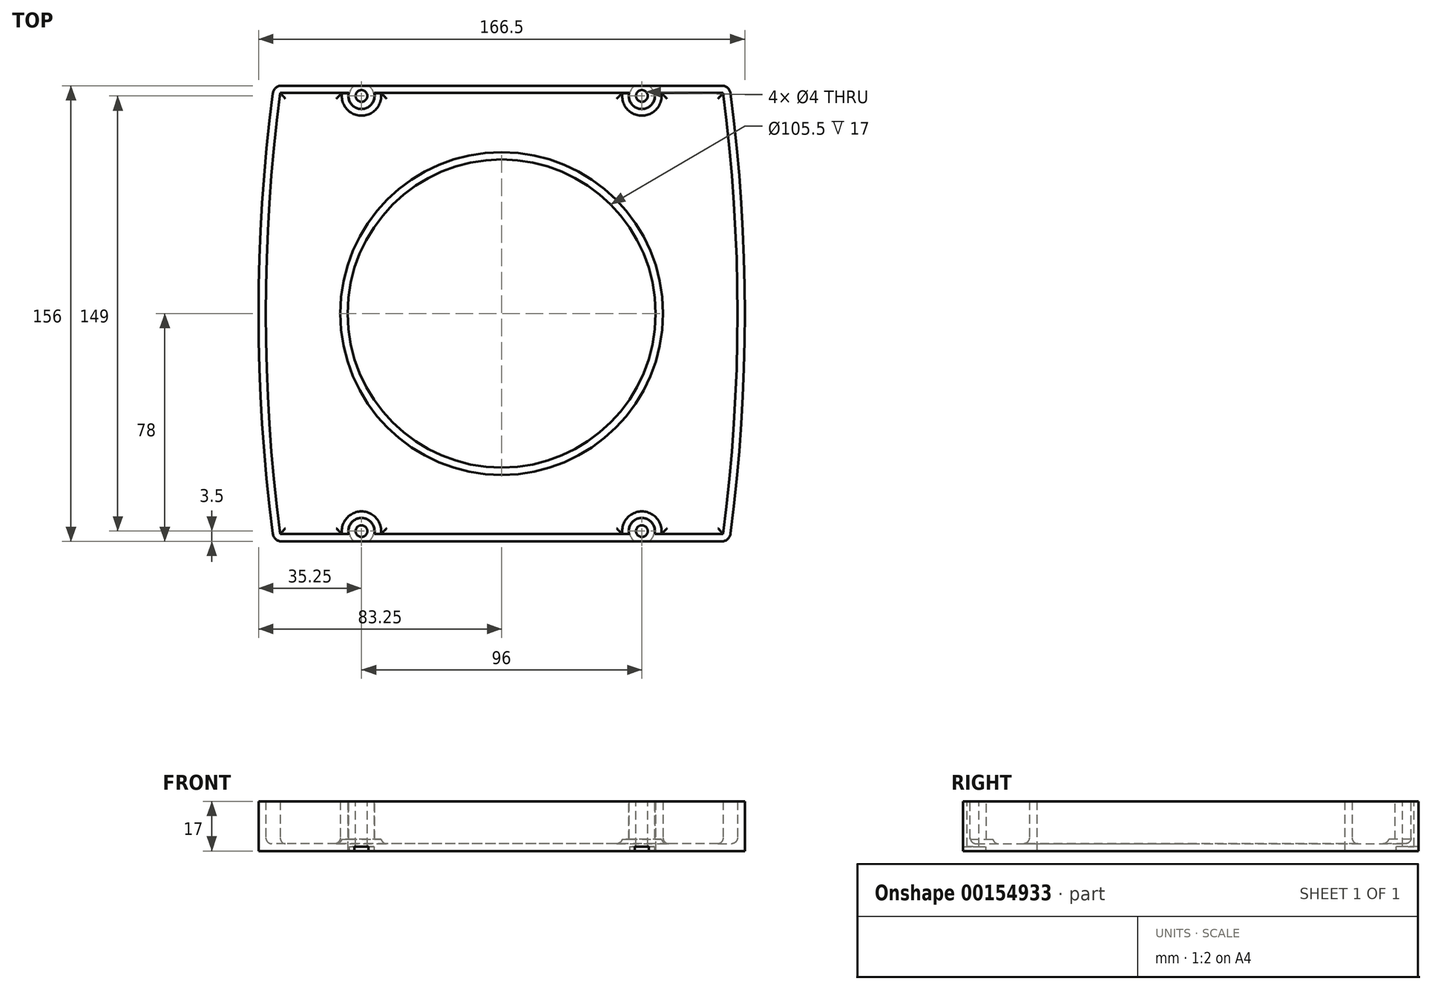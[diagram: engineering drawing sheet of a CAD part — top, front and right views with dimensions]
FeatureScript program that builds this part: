
annotation { "Feature Type Name" : "Feature", "Feature Type Description" : "" }
export const myFeature = defineFeature(function(context is Context, id is Id, definition is map)
    precondition{}
    {
        {
            var Q0;
            Q0=qCreatedBy(makeId("Top.planeOp"),FACE);
            var sketch = newSketch(context, id + "F0", { "sketchPlane" : qUnion([Q0])});
            skLineSegment(sketch, "E0.bottom", {"start": v(78, 78) * mm, "end": v(-78, 78) * mm});
            skLineSegment(sketch, "E0.top", {"start": v(78, -78) * mm, "end": v(-78, -78) * mm});
            skPoint(sketch, "E0.middle", {"position": v(0, 0) * mm});
            skCircle(sketch, "E1", {"center": v(0, 0) * mm, "radius": 52.75 * mm});
            skArc(sketch, "E2", {"start": v(-78, 78) * mm, "mid": v(-83.25, 0) * mm, "end": v(-78, -78) * mm});
            skArc(sketch, "E3.MirrorCS", {"start": v(78, 78) * mm, "mid": v(83.25, 0) * mm, "end": v(78, -78) * mm});
            skSolve(sketch);
        }
        {
            var Q0;
            Q0=makeQuery(id+"F0.imprint","IMPRINT",FACE,{"disambiguationData":[TD([[makeQuery(id+"F0.imprint","IMPRINT",EDGE,{"derivedFrom":sQuery(id+"F0.wireOp",EDGE,"E0.bottom")}),1.0]])]});
            extrude(context, id + "F1", {"entities" : qUnion([Q0]), "depth" : 17 * mm});
        }
        {
            var Q0;
            Q0=makeQuery(id+"F1.opExtrude","CAP_FACE",FACE,{"disambiguationData":[OSD([sQuery(id+"F0.wireOp",EDGE,"E0.bottom"),sQuery(id+"F0.wireOp",EDGE,"E0.top"),sQuery(id+"F0.wireOp",EDGE,"E1"),sQuery(id+"F0.wireOp",EDGE,"E2"),sQuery(id+"F0.wireOp",EDGE,"E3.MirrorCS")])],"isStart":false});
            var sketch = newSketch(context, id + "F2", { "sketchPlane" : qUnion([Q0])});
            skCircle(sketch, "E4", {"center": v(48, -74.5) * mm, "radius": 2 * mm});
            skCircle(sketch, "E5.MirrorC", {"center": v(-48, -74.5) * mm, "radius": 2 * mm});
            skCircle(sketch, "E6.MirrorC", {"center": v(-48, 74.5) * mm, "radius": 2 * mm});
            skCircle(sketch, "E7.MirrorC", {"center": v(48, 74.5) * mm, "radius": 2 * mm});
            skSolve(sketch);
        }
        {
            var Q0;
            Q0 = qSketchRegion(id + "F2", true);
            extrude(context, id + "F3", {"entities" : qUnion([Q0]), "operationType" : NewBodyOperationType.REMOVE, "oppositeDirection" : true, "depth" : 25 * mm});
        }
        {
            var Q0;
            Q0=makeQuery(id+"F1.opExtrude","CAP_FACE",FACE,{"disambiguationData":[OSD([sQuery(id+"F0.wireOp",EDGE,"E0.bottom"),sQuery(id+"F0.wireOp",EDGE,"E0.top"),sQuery(id+"F0.wireOp",EDGE,"E1"),sQuery(id+"F0.wireOp",EDGE,"E2"),sQuery(id+"F0.wireOp",EDGE,"E3.MirrorCS")])],"isStart":true});
            var sketch = newSketch(context, id + "F4", { "sketchPlane" : qUnion([Q0])});
            skCircle(sketch, "E8", {"center": v(48, -74.5) * mm, "radius": 4.25 * mm});
            skCircle(sketch, "E9.MirrorC", {"center": v(-48, -74.5) * mm, "radius": 4.25 * mm});
            skCircle(sketch, "E10.MirrorC", {"center": v(48, 74.5) * mm, "radius": 4.25 * mm});
            skCircle(sketch, "E11.MirrorC", {"center": v(-48, 74.5) * mm, "radius": 4.25 * mm});
            skSolve(sketch);
        }
        {
            var Q0;
            Q0 = qSketchRegion(id + "F4", true);
            extrude(context, id + "F5", {"entities" : qUnion([Q0]), "operationType" : NewBodyOperationType.REMOVE, "oppositeDirection" : true, "depth" : 1.5 * mm});
        }
        {
            var Q0;
            Q0=makeQuery(id+"F1.opExtrude","CAP_FACE",FACE,{"disambiguationData":[OSD([sQuery(id+"F0.wireOp",EDGE,"E0.bottom"),sQuery(id+"F0.wireOp",EDGE,"E0.top"),sQuery(id+"F0.wireOp",EDGE,"E1"),sQuery(id+"F0.wireOp",EDGE,"E2"),sQuery(id+"F0.wireOp",EDGE,"E3.MirrorCS")])],"isStart":false});
            shell(context, id + "F6", {"entities" : qUnion([Q0]), "thickness" : 2.5 * mm});
        }
        {
            var Q0;
            Q0=makeQuery(id+"F1.opExtrude","SWEPT_EDGE",EDGE,{"disambiguationData":[OSD([sQuery(id+"F0.wireOp",EDGE,"E0.top"),sQuery(id+"F0.wireOp",EDGE,"E2")])]});
            var Q1;
            Q1=makeQuery(id+"F1.opExtrude","SWEPT_EDGE",EDGE,{"disambiguationData":[OSD([sQuery(id+"F0.wireOp",EDGE,"E0.top"),sQuery(id+"F0.wireOp",EDGE,"E3.MirrorCS")])]});
            var Q2;
            Q2=makeQuery(id+"F1.opExtrude","SWEPT_EDGE",EDGE,{"disambiguationData":[OSD([sQuery(id+"F0.wireOp",EDGE,"E0.bottom"),sQuery(id+"F0.wireOp",EDGE,"E3.MirrorCS")])]});
            var Q3;
            Q3=makeQuery(id+"F1.opExtrude","SWEPT_EDGE",EDGE,{"disambiguationData":[OSD([sQuery(id+"F0.wireOp",EDGE,"E0.bottom"),sQuery(id+"F0.wireOp",EDGE,"E2")])]});
            fillet(context, id + "F7", {"entities" : qUnion([Q0, Q1, Q2, Q3]), "radius" : 3 * mm, "tangentPropagation" : true, "allowEdgeOverflow" : false});
        }
        {
            var Q0;
            {var subQ0=sQuery(id+"F0.wireOp",EDGE,"E3.MirrorCS");var subQ1=sQuery(id+"F0.wireOp",EDGE,"E2");var subQ2=sQuery(id+"F0.wireOp",EDGE,"E1");var subQ3=sQuery(id+"F0.wireOp",EDGE,"E0.top");var subQ4=sQuery(id+"F0.wireOp",EDGE,"E0.bottom");Q0=makeQuery(id+"F6.opShell","OFFSET_FACE",FACE,{"disambiguationData":[OSD([subQ4,subQ3,subQ2,subQ1,subQ0]),TDD([makeQuery(id+"F1.opExtrude","CAP_FACE",FACE,{"disambiguationData":[OSD([subQ4,subQ3,subQ2,subQ1,subQ0])],"isStart":true})])]});}
            fillet(context, id + "F8", {"entities" : qUnion([Q0]), "radius" : 2 * mm, "tangentPropagation" : true, "allowEdgeOverflow" : false});
        }
    });
